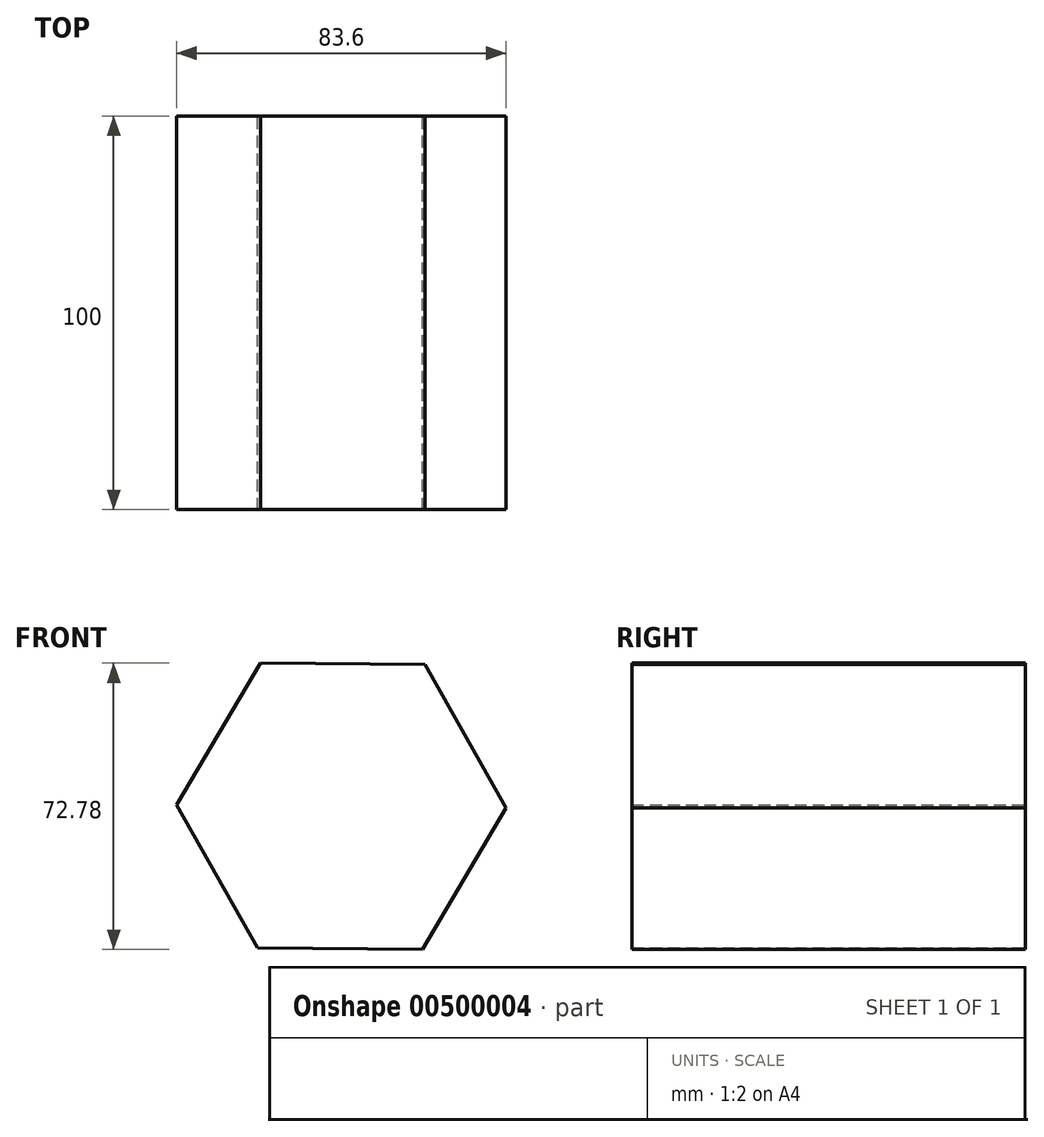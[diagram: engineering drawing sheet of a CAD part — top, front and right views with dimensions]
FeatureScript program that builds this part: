
annotation { "Feature Type Name" : "Feature", "Feature Type Description" : "" }
export const myFeature = defineFeature(function(context is Context, id is Id, definition is map)
    precondition{}
    {
        {
            var Q0;
            Q0=qCreatedBy(makeId("Front.planeOp"),FACE);
            var sketch = newSketch(context, id + "F0", { "sketchPlane" : qUnion([Q0])});
            skCircle(sketch, "E0.cCircle", {"center": v(0, 0) * mm, "radius": 41.8 * mm, "construction": true});
            skLineSegment(sketch, "E0.0", {"start": v(-20.57, 36.39) * mm, "end": v(21.23, 36) * mm});
            skLineSegment(sketch, "E0.1", {"start": v(21.23, 36) * mm, "end": v(41.8, -0.38) * mm});
            skLineSegment(sketch, "E0.2", {"start": v(41.8, -0.38) * mm, "end": v(20.57, -36.39) * mm});
            skLineSegment(sketch, "E0.3", {"start": v(20.57, -36.39) * mm, "end": v(-21.23, -36) * mm});
            skLineSegment(sketch, "E0.4", {"start": v(-21.23, -36) * mm, "end": v(-41.8, 0.38) * mm});
            skLineSegment(sketch, "E0.5", {"start": v(-41.8, 0.38) * mm, "end": v(-20.57, 36.39) * mm});
            skSolve(sketch);
        }
        {
            var Q0;
            Q0 = qSketchRegion(id + "F0", true);
            extrude(context, id + "F1", {"entities" : qUnion([Q0]), "endBound" : BoundingType.SYMMETRIC, "depth" : 100 * mm});
        }
    });
